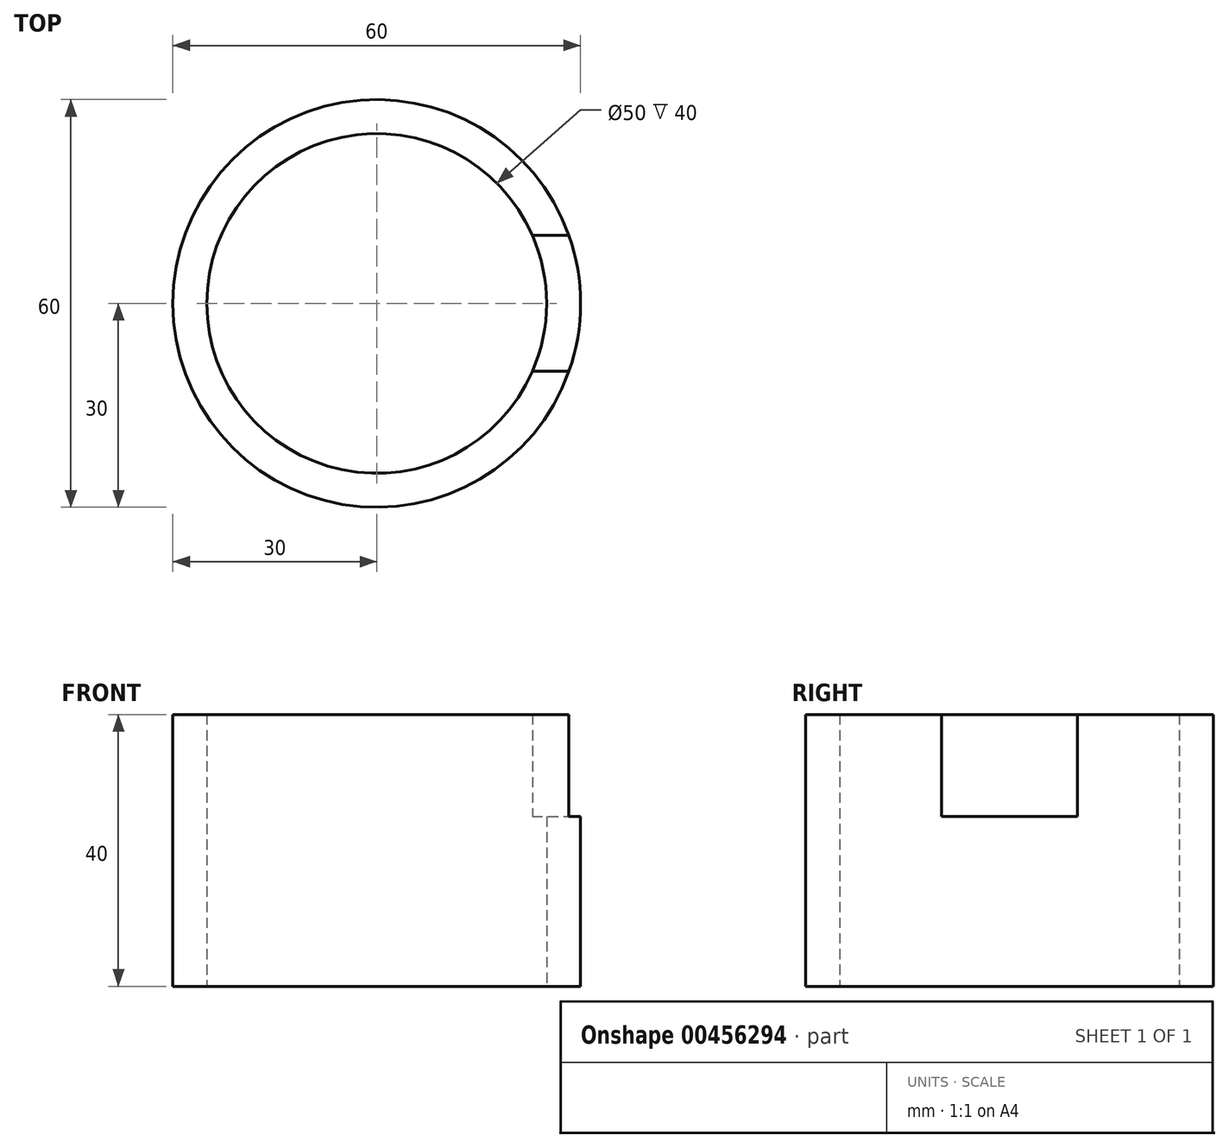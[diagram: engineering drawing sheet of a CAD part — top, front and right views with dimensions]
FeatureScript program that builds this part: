
annotation { "Feature Type Name" : "Feature", "Feature Type Description" : "" }
export const myFeature = defineFeature(function(context is Context, id is Id, definition is map)
    precondition{}
    {
        {
            var Q0;
            Q0=qCreatedBy(makeId("Top.planeOp"),FACE);
            var sketch = newSketch(context, id + "F0", { "sketchPlane" : qUnion([Q0])});
            skArc(sketch, "E0", {"start": v(58.28, 40) * mm, "mid": v(0, 30) * mm, "end": v(58.28, 20) * mm});
            skArc(sketch, "E1", {"start": v(52.91, 40) * mm, "mid": v(5, 30) * mm, "end": v(52.91, 20) * mm});
            skLineSegment(sketch, "E2", {"start": v(52.91, 40) * mm, "end": v(58.28, 40) * mm});
            skLineSegment(sketch, "E3", {"start": v(52.91, 20) * mm, "end": v(58.28, 20) * mm});
            skCircle(sketch, "E4", {"center": v(30, 30) * mm, "radius": 25 * mm});
            skCircle(sketch, "E5", {"center": v(30, 30) * mm, "radius": 30 * mm});
            skSolve(sketch);
        }
        {
            var Q0;
            {var subQ0=sQuery(id+"F0.wireOp",EDGE,"E2");Q0=makeQuery(id+"F0.imprint","IMPRINT",FACE,{"disambiguationData":[TD([[makeQuery(id+"F0.imprint","IMPRINT",EDGE,{"derivedFrom":subQ0}),1.0]])]});}
            extrude(context, id + "F1", {"entities" : qUnion([Q0]), "depth" : 40 * mm});
        }
        {
            var Q0;
            Q0=qSketchRegion(id+"F0",true);
            extrude(context, id + "F2", {"entities" : qUnion([Q0]), "operationType" : NewBodyOperationType.ADD, "depth" : 25 * mm});
        }
    });
